# Revit family: P506QL
name_source: partatom
category: Generic Models
revit_build: Autodesk Revit 2018 (Build: 20170223_1515(x64)
units: mm (PartAtom-declared; Revit-internal decimal feet)

## family parameters
Always vertical = Yes
Can host rebar = No
Cut with Voids When Loaded = No
OmniClass Number = 23.80.30.11.17
Part Type = Normal
Room Calculation Point = No
Round Connector Dimension = Use Diameter
Shared = No
Work Plane-Based = No

## types (1)
- P506QL
    (ECO Mode Off/ECO Mode/Network Standby/ = 580W / 330W / 2W / 0.5W
    Built-in Speaker = 10W
    Contrast Ratio (up to) = 500,000:1
    Description = 4K UHD (3840 x 2160)
    Display Technology = DLP (0.47" DMD)
    External Control = RS-232 (D-Sub 9pin), IR, RJ45
    Fan Noise = 35dB (ECO mode Off), 32dB (ECO mode)
    Gross Weight = 32.0 lbs. (14.5 kg)
    Humidity = 20-80% non-condensing
    Input Current = 6A
    Input Terminals - Audio1 = Stereo Mini Jack
    Input Terminals - RGB1 (analog) = VGA 15-pin D-sub
    Input Terminals - RGB2 (digital) = HDMI w/ HDCP (v2.2)
    Input Terminals - RGB3 (digital) = HDMI w/ HDCP (v2.2)
    Input Terminals - RGB4 (digital) = HDBaseT
    Installation Orientation = Floor/Front, Floor/Rear, Ceiling/Front, Ceiling/Rear
    Keystone Correction = Vertical
    Laser Life (50%) = 20,000 hours
    Lens - F-number, focal length = F=1.8~2.43 / f=12.1~18.1mm
    Lens - Focus = Manual
    Lens - Shift = Manual (H = +/- 20% / V = -+/- 60)
    Lens - Throw Ratio = 1.127 - 1.697:1
    Lens - Zoom = Manual
    Lens - Zoom Ratio = 1.5x
    Light Output (lumens) - Center = 5200
    Light Output (lumens) - ECO mode OFF = 5000
    Light Output (lumens) - ECo mode = 3000
    Macintosh Compatibility = Yes
    Manufacturer = NEC
    Model = P506QL
    Net Weight = 25.4 lbs. (11.5 kg)
    Operating Temperature = 41-104°F / 5-40°C
    Output Terminals - 3D Sync = mini DIN 3-pin
    Output Terminals - Audio Out = Stero Mini Jack
    Power Requirements = 100-240V AC, 50/60 Hz
    Product Dimensions (WxHxD) = 18.9 x 6.8 x 15.7 in. (480 x 172 x 400 mm)
    Projection Angle = 25.46° tele / 34.5° wide
    Projection Distance = 5.2 - 26.2 ft. / 1.6 - 8m
    Regulations = UL60950-1:2nd edition,2014, UL62368-1:2nd Edition, UL62368-1:3rd Edition, FDA, FCC 
Part15 Subpart B(ANSI C63.4:2014), Proposition65, TPCH, CAN/CSA C22.2 No.62368-1-14,2nd 
Edition,2014, ICES-003 Issue6(ANSI C63.4:2014)
    Resolution - Maximum = Up to 4K@60Hz (3840x2160) for HDMI
    Resolution - Native = 4K UHD (3840 x 2160)
    SD/HD Video Signal Compatibility = VGA, SVGA, XGA, WXGA, Quad-VGA, SXGA, SXGA+, WXGA+, UXGA, WSXGA+, HD, FHD
    Screen Size (diagonal) = 50 - 310 in. / 1.27 - 7.87m
    Shipping Dimensions (WxHxD) = 23.2 x 11.7 x 19.3 in. (590 x 297 x 490 mm)
    Storage = 14° – 122°F / -10° – 50°C
    Synchronization Correction - Horizontal = 15.734KHz ~ 153kHz (RGB: Hz, 24 ~ 100KHz)
    Synchronization Range - Vertical = 48 ~ 100, 120Hz
    Type Image = <None>
    URL = www.sharpnecdisplays.us
    USB - Mini = Service
    USB - Type A = 5V/2.0A power
    Wired LAN port = RJ45 (100Base-TX/10Base-T)

## geometry (parser evidence)
native form markers: Sweep x2
no freeform markers — native parametric forms only
